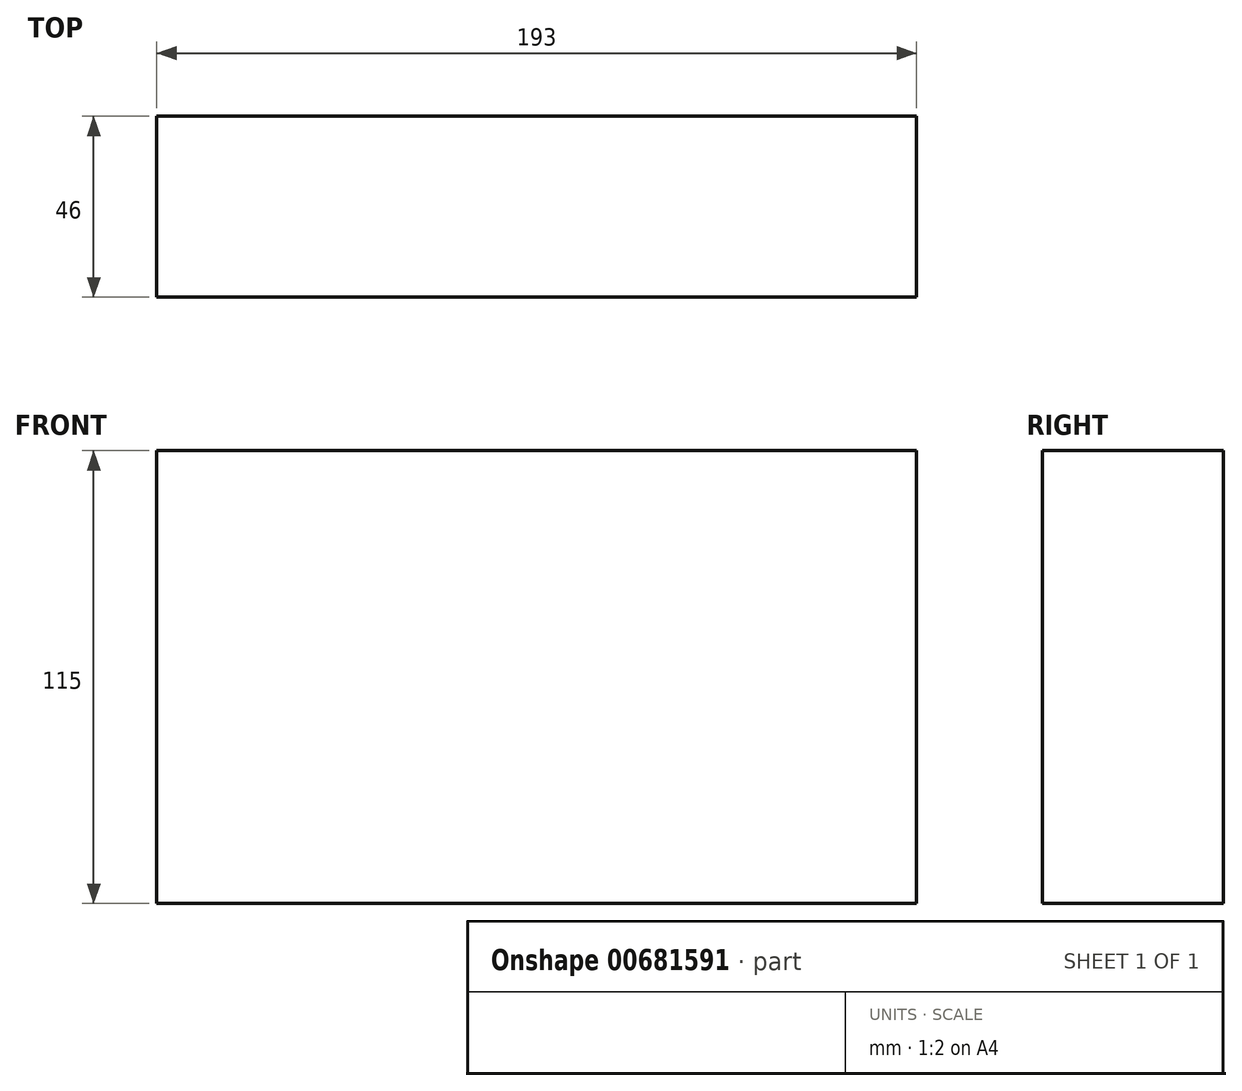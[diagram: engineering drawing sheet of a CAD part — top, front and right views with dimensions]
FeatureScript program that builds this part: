
annotation { "Feature Type Name" : "Feature", "Feature Type Description" : "" }
export const myFeature = defineFeature(function(context is Context, id is Id, definition is map)
    precondition{}
    {
        {
            var Q0;
            Q0=qCreatedBy(makeId("Front.planeOp"),FACE);
            var sketch = newSketch(context, id + "F0", { "sketchPlane" : qUnion([Q0])});
            skLineSegment(sketch, "E0.bottom", {"start": v(-234.43, 99.5) * mm, "end": v(-41.43, 99.5) * mm});
            skLineSegment(sketch, "E0.top", {"start": v(-234.43, -15.5) * mm, "end": v(-41.43, -15.5) * mm});
            skLineSegment(sketch, "E0.left", {"start": v(-234.43, 99.5) * mm, "end": v(-234.43, -15.5) * mm});
            skLineSegment(sketch, "E0.right", {"start": v(-41.43, 99.5) * mm, "end": v(-41.43, -15.5) * mm});
            skSolve(sketch);
        }
        {
            var Q0;
            Q0 = qSketchRegion(id + "F0", true);
            extrude(context, id + "F1", {"entities" : qUnion([Q0]), "depth" : 46 * mm, "offsetDistance" : 25 * mm});
        }
    });
